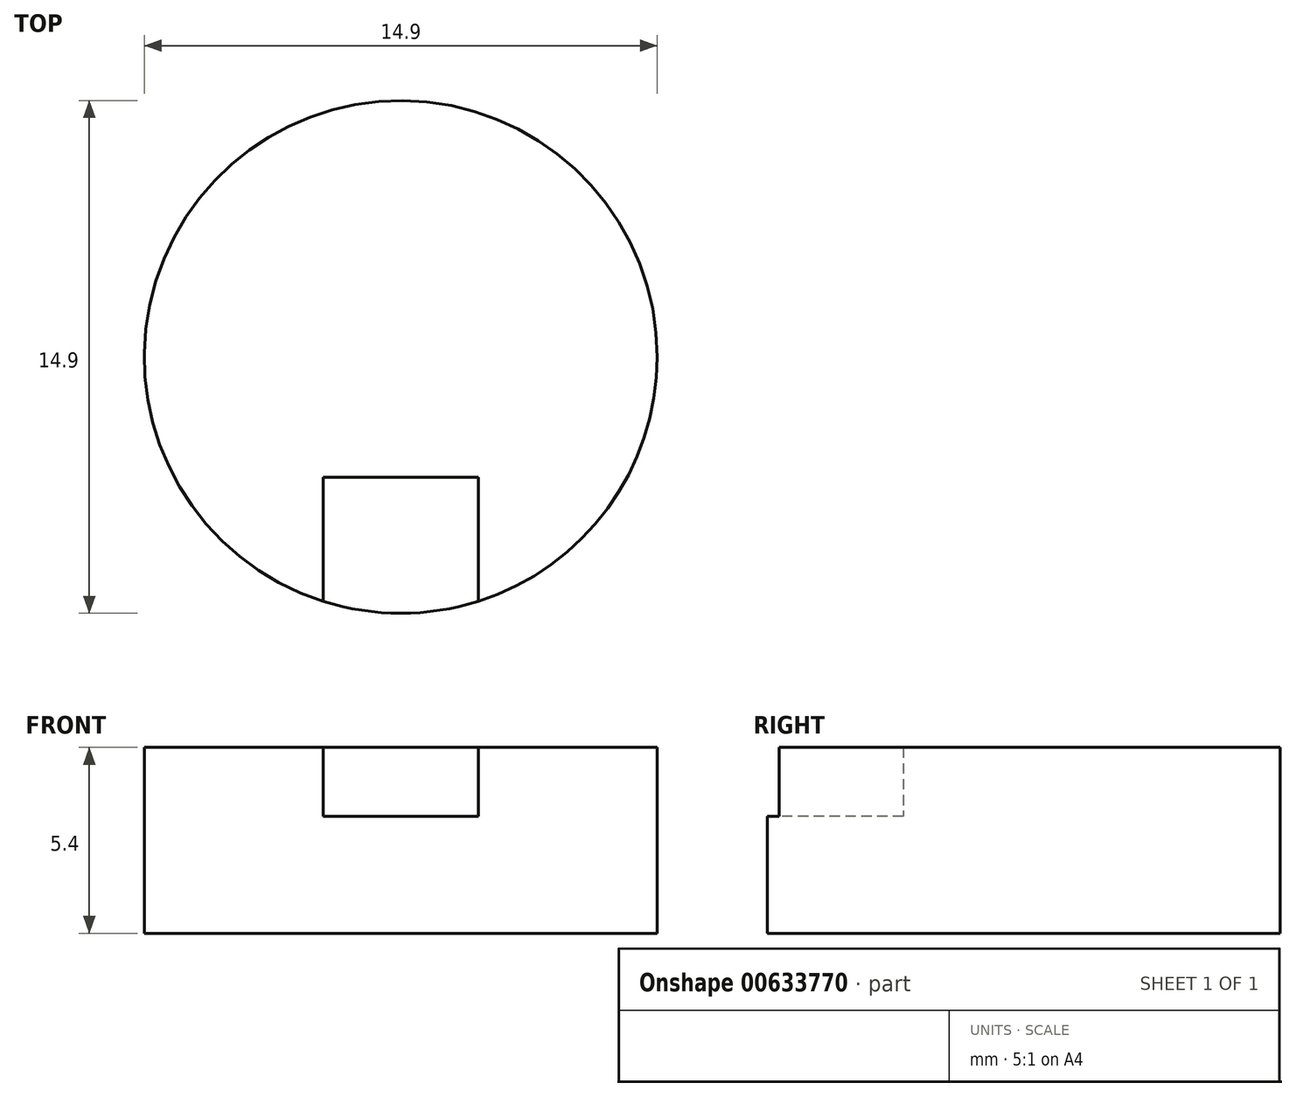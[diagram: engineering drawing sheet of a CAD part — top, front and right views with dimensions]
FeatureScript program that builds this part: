
annotation { "Feature Type Name" : "Feature", "Feature Type Description" : "" }
export const myFeature = defineFeature(function(context is Context, id is Id, definition is map)
    precondition{}
    {
        {
            var Q0;
            Q0=qCreatedBy(makeId("Top.planeOp"),FACE);
            var sketch = newSketch(context, id + "F0", { "sketchPlane" : qUnion([Q0])});
            skArc(sketch, "E0", {"start": v(2.25, -7.1) * mm, "mid": v(0, 7.45) * mm, "end": v(-2.25, -7.1) * mm});
            skLineSegment(sketch, "E1", {"start": v(-16.45, -5) * mm, "end": v(27.1, -5) * mm, "construction": true});
            skLineSegment(sketch, "E2.top", {"start": v(2.25, -3.5) * mm, "end": v(-2.25, -3.5) * mm});
            skLineSegment(sketch, "E2.left", {"start": v(2.25, -6.5) * mm, "end": v(2.25, -3.5) * mm});
            skLineSegment(sketch, "E2.right", {"start": v(-2.25, -6.5) * mm, "end": v(-2.25, -3.5) * mm});
            skPoint(sketch, "E2.middle", {"position": v(0, -5) * mm});
            skLineSegment(sketch, "E3", {"start": v(-2.25, -6.5) * mm, "end": v(-2.25, -7.1) * mm});
            skLineSegment(sketch, "E4", {"start": v(2.25, -6.5) * mm, "end": v(2.25, -7.1) * mm});
            skSolve(sketch);
        }
        {
            var Q0;
            Q0=qCreatedBy(makeId("Top.planeOp"),FACE);
            var sketch = newSketch(context, id + "F1", { "sketchPlane" : qUnion([Q0])});
            skCircle(sketch, "E5", {"center": v(0, 0) * mm, "radius": 7.45 * mm});
            skSolve(sketch);
        }
        {
            var Q0;
            Q0 = qSketchRegion(id + "F1", true);
            extrude(context, id + "F2", {"entities" : qUnion([Q0]), "oppositeDirection" : true, "depth" : 3.4 * mm, "offsetDistance" : 25 * mm});
        }
        {
            var Q0;
            Q0 = qSketchRegion(id + "F0", true);
            extrude(context, id + "F3", {"entities" : qUnion([Q0]), "operationType" : NewBodyOperationType.ADD, "depth" : 2 * mm, "offsetDistance" : 25 * mm});
        }
    });
